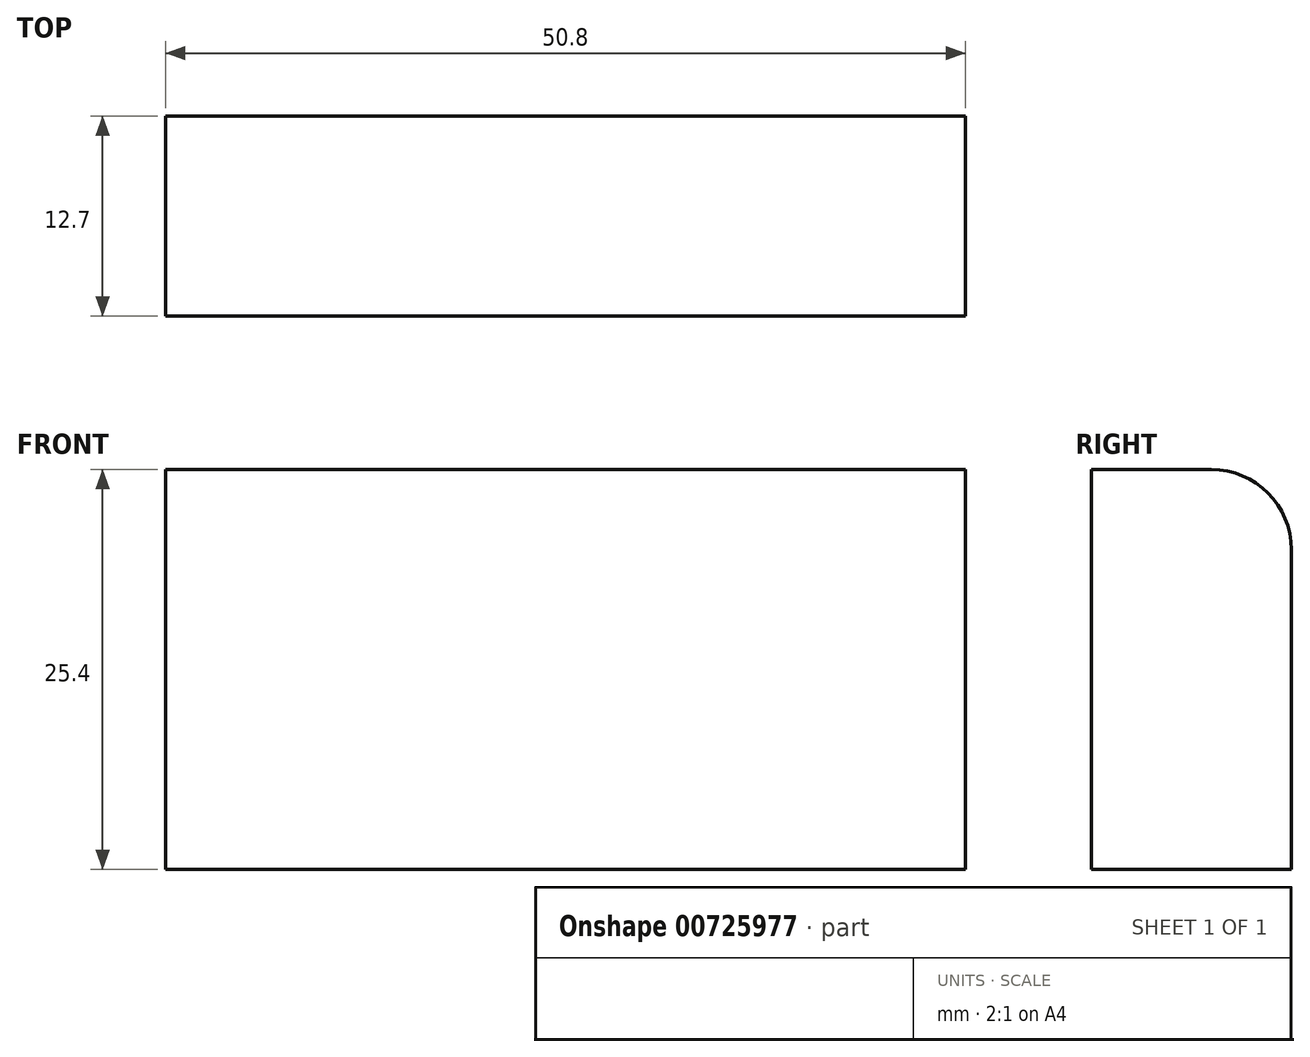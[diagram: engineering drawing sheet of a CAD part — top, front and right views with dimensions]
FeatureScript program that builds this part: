
annotation { "Feature Type Name" : "Feature", "Feature Type Description" : "" }
export const myFeature = defineFeature(function(context is Context, id is Id, definition is map)
    precondition{}
    {
        {
            var Q0;
            Q0=qCreatedBy(makeId("Front.planeOp"),FACE);
            var sketch = newSketch(context, id + "F0", { "sketchPlane" : qUnion([Q0])});
            skLineSegment(sketch, "E0.bottom", {"start": v(0, 0) * mm, "end": v(50.8, 0) * mm});
            skLineSegment(sketch, "E0.top", {"start": v(0, 25.4) * mm, "end": v(50.8, 25.4) * mm});
            skLineSegment(sketch, "E0.left", {"start": v(0, 0) * mm, "end": v(0, 25.4) * mm});
            skLineSegment(sketch, "E0.right", {"start": v(50.8, 0) * mm, "end": v(50.8, 25.4) * mm});
            skSolve(sketch);
        }
        {
            var Q0;
            Q0=makeQuery(id+"F0.imprint","IMPRINT",FACE,{"disambiguationData":[TD([[makeQuery(id+"F0.imprint","IMPRINT",EDGE,{"derivedFrom":sQuery(id+"F0.wireOp",EDGE,"E0.bottom")}),1.0]])]});
            extrude(context, id + "F1", {"entities" : qUnion([Q0]), "depth" : 12.7 * mm, "offsetDistance" : 25.4 * mm});
        }
        {
            var Q0;
            Q0=makeQuery(id+"F1.opExtrude","CAP_EDGE",EDGE,{"disambiguationData":[OSD([sQuery(id+"F0.wireOp",EDGE,"E0.top")])],"isStart":true});
            fillet(context, id + "F2", {"entities" : qUnion([Q0]), "radius" : 5.08 * mm, "tangentPropagation" : true, "allowEdgeOverflow" : false});
        }
    });
